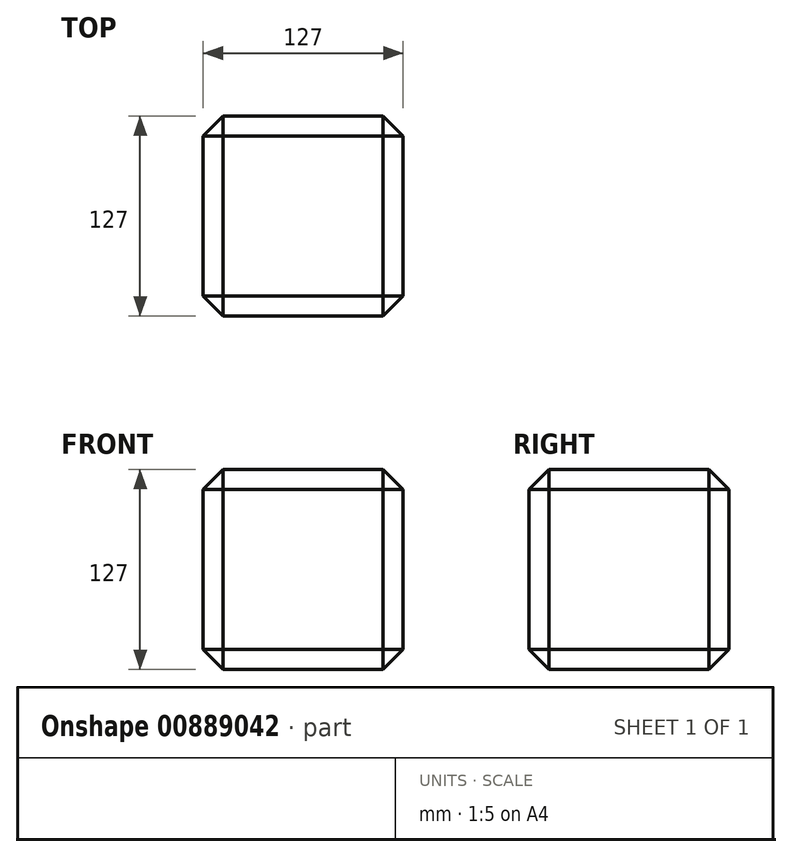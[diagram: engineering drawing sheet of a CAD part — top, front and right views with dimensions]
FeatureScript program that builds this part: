
annotation { "Feature Type Name" : "Feature", "Feature Type Description" : "" }
export const myFeature = defineFeature(function(context is Context, id is Id, definition is map)
    precondition{}
    {
        {
            var Q0;
            Q0=qCreatedBy(makeId("Front.planeOp"),FACE);
            var sketch = newSketch(context, id + "F0", { "sketchPlane" : qUnion([Q0])});
            skLineSegment(sketch, "E0.bottom", {"start": v(63.5, 63.5) * mm, "end": v(-63.5, 63.5) * mm});
            skLineSegment(sketch, "E0.top", {"start": v(63.5, -63.5) * mm, "end": v(-63.5, -63.5) * mm});
            skLineSegment(sketch, "E0.left", {"start": v(63.5, 63.5) * mm, "end": v(63.5, -63.5) * mm});
            skLineSegment(sketch, "E0.right", {"start": v(-63.5, 63.5) * mm, "end": v(-63.5, -63.5) * mm});
            skPoint(sketch, "E0.middle", {"position": v(0, 0) * mm});
            skSolve(sketch);
        }
        {
            var Q0;
            Q0=makeQuery(id+"F0.imprint","IMPRINT",FACE,{"disambiguationData":[TD([[makeQuery(id+"F0.imprint","IMPRINT",EDGE,{"derivedFrom":sQuery(id+"F0.wireOp",EDGE,"E0.bottom")}),1.0]])]});
            extrude(context, id + "F1", {"entities" : qUnion([Q0]), "oppositeDirection" : true, "depth" : 127 * mm, "offsetDistance" : 25.4 * mm});
        }
        {
            var Q0;
            Q0=makeQuery(id+"F1.opExtrude","SWEPT_EDGE",EDGE,{"disambiguationData":[OSD([sQuery(id+"F0.wireOp",EDGE,"E0.bottom"),sQuery(id+"F0.wireOp",EDGE,"E0.right")])]});
            var Q1;
            Q1=makeQuery(id+"F1.opExtrude","CAP_EDGE",EDGE,{"disambiguationData":[OSD([sQuery(id+"F0.wireOp",EDGE,"E0.right")])],"isStart":false});
            var Q2;
            Q2=makeQuery(id+"F1.opExtrude","CAP_EDGE",EDGE,{"disambiguationData":[OSD([sQuery(id+"F0.wireOp",EDGE,"E0.bottom")])],"isStart":false});
            var Q3;
            Q3=makeQuery(id+"F1.opExtrude","CAP_EDGE",EDGE,{"disambiguationData":[OSD([sQuery(id+"F0.wireOp",EDGE,"E0.bottom")])],"isStart":true});
            var Q4;
            Q4=makeQuery(id+"F1.opExtrude","CAP_EDGE",EDGE,{"disambiguationData":[OSD([sQuery(id+"F0.wireOp",EDGE,"E0.right")])],"isStart":true});
            var Q5;
            Q5=makeQuery(id+"F1.opExtrude","CAP_EDGE",EDGE,{"disambiguationData":[OSD([sQuery(id+"F0.wireOp",EDGE,"E0.top")])],"isStart":true});
            var Q6;
            Q6=makeQuery(id+"F1.opExtrude","SWEPT_EDGE",EDGE,{"disambiguationData":[OSD([sQuery(id+"F0.wireOp",EDGE,"E0.top"),sQuery(id+"F0.wireOp",EDGE,"E0.left")])]});
            var Q7;
            Q7=makeQuery(id+"F1.opExtrude","CAP_EDGE",EDGE,{"disambiguationData":[OSD([sQuery(id+"F0.wireOp",EDGE,"E0.left")])],"isStart":true});
            var Q8;
            Q8=makeQuery(id+"F1.opExtrude","SWEPT_EDGE",EDGE,{"disambiguationData":[OSD([sQuery(id+"F0.wireOp",EDGE,"E0.bottom"),sQuery(id+"F0.wireOp",EDGE,"E0.left")])]});
            var Q9;
            Q9=makeQuery(id+"F1.opExtrude","CAP_EDGE",EDGE,{"disambiguationData":[OSD([sQuery(id+"F0.wireOp",EDGE,"E0.left")])],"isStart":false});
            var Q10;
            Q10=makeQuery(id+"F1.opExtrude","SWEPT_EDGE",EDGE,{"disambiguationData":[OSD([sQuery(id+"F0.wireOp",EDGE,"E0.top"),sQuery(id+"F0.wireOp",EDGE,"E0.right")])]});
            var Q11;
            Q11=makeQuery(id+"F1.opExtrude","CAP_EDGE",EDGE,{"disambiguationData":[OSD([sQuery(id+"F0.wireOp",EDGE,"E0.top")])],"isStart":false});
            chamfer(context, id + "F2", {"entities" : qUnion([Q0, Q1, Q2, Q3, Q4, Q5, Q6, Q7, Q8, Q9, Q10, Q11]), "width" : 12.7 * mm, "tangentPropagation" : true});
        }
    });
